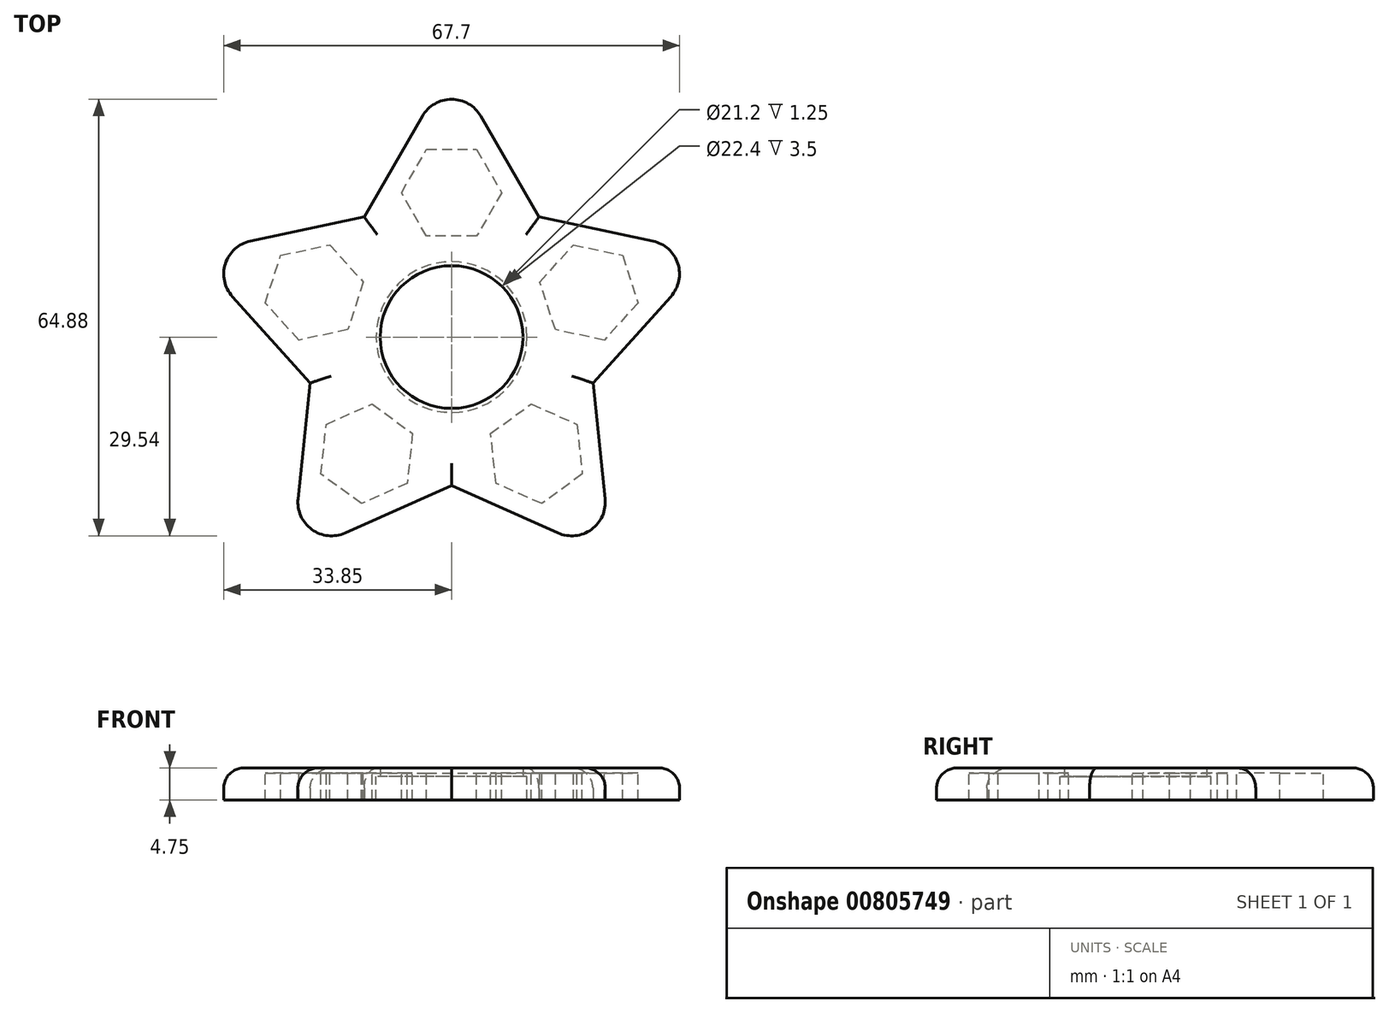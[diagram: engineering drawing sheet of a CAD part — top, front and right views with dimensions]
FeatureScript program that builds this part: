
annotation { "Feature Type Name" : "Feature", "Feature Type Description" : "" }
export const myFeature = defineFeature(function(context is Context, id is Id, definition is map)
    precondition{}
    {
        {
            var Q0;
            Q0=qCreatedBy(makeId("Top.planeOp"),FACE);
            var sketch = newSketch(context, id + "F0", { "sketchPlane" : qUnion([Q0])});
            skCircle(sketch, "E0.cCircle", {"center": v(0, 0) * mm, "radius": 15 * mm, "construction": true});
            skLineSegment(sketch, "E0.0", {"start": v(10.9, -15) * mm, "end": v(-10.9, -15) * mm, "construction": true});
            skLineSegment(sketch, "E0.1", {"start": v(-10.9, -15) * mm, "end": v(-17.63, 5.73) * mm, "construction": true});
            skLineSegment(sketch, "E0.2", {"start": v(-17.63, 5.73) * mm, "end": v(0, 18.54) * mm, "construction": true});
            skLineSegment(sketch, "E0.3", {"start": v(0, 18.54) * mm, "end": v(17.63, 5.73) * mm, "construction": true});
            skLineSegment(sketch, "E0.4", {"start": v(17.63, 5.73) * mm, "end": v(10.9, -15) * mm, "construction": true});
            skPoint(sketch, "E0.0.midPoint", {"position": v(0, -15) * mm});
            skCircle(sketch, "E1", {"center": v(0, 0) * mm, "radius": 11.2 * mm});
            skLineSegment(sketch, "E2", {"start": v(0, 0) * mm, "end": v(-17.63, 5.73) * mm, "construction": true});
            skLineSegment(sketch, "E3", {"start": v(-17.63, 5.73) * mm, "end": v(-45.65, 14.83) * mm, "construction": true});
            skLineSegment(sketch, "E4", {"start": v(0, 0) * mm, "end": v(0, 18.54) * mm, "construction": true});
            skLineSegment(sketch, "E5", {"start": v(0, 18.54) * mm, "end": v(0, 45.62) * mm, "construction": true});
            skLineSegment(sketch, "E6", {"start": v(0, 0) * mm, "end": v(17.63, 5.73) * mm, "construction": true});
            skLineSegment(sketch, "E7", {"start": v(17.63, 5.73) * mm, "end": v(64.66, 21) * mm, "construction": true});
            skLineSegment(sketch, "E8", {"start": v(0, 0) * mm, "end": v(10.9, -15) * mm, "construction": true});
            skLineSegment(sketch, "E9", {"start": v(10.9, -15) * mm, "end": v(33.3, -45.85) * mm, "construction": true});
            skLineSegment(sketch, "E10", {"start": v(0, 0) * mm, "end": v(-10.9, -15) * mm, "construction": true});
            skLineSegment(sketch, "E11", {"start": v(-10.9, -15) * mm, "end": v(-35.87, -49.38) * mm, "construction": true});
            skCircle(sketch, "E12.cCircle", {"center": v(0, 21.45) * mm, "radius": 6.44 * mm, "construction": true});
            skLineSegment(sketch, "E12.0", {"start": v(3.72, 15) * mm, "end": v(-3.72, 15) * mm});
            skLineSegment(sketch, "E12.1", {"start": v(-3.72, 15) * mm, "end": v(-7.44, 21.45) * mm});
            skLineSegment(sketch, "E12.2", {"start": v(-7.44, 21.45) * mm, "end": v(-3.72, 27.9) * mm});
            skLineSegment(sketch, "E12.3", {"start": v(-3.72, 27.9) * mm, "end": v(3.72, 27.89) * mm});
            skLineSegment(sketch, "E12.4", {"start": v(3.72, 27.89) * mm, "end": v(7.44, 21.44) * mm});
            skLineSegment(sketch, "E12.5", {"start": v(7.44, 21.44) * mm, "end": v(3.72, 15) * mm});
            skPoint(sketch, "E12.0.midPoint", {"position": v(0, 15) * mm});
            skCircle(sketch, "E13.cCircle", {"center": v(20.4, 6.63) * mm, "radius": 6.44 * mm, "construction": true});
            skLineSegment(sketch, "E13.0", {"start": v(15.42, 1.1) * mm, "end": v(13.12, 8.17) * mm});
            skLineSegment(sketch, "E13.1", {"start": v(13.12, 8.17) * mm, "end": v(18.1, 13.7) * mm});
            skLineSegment(sketch, "E13.2", {"start": v(18.1, 13.7) * mm, "end": v(25.38, 12.16) * mm});
            skLineSegment(sketch, "E13.3", {"start": v(25.38, 12.16) * mm, "end": v(27.67, 5.08) * mm});
            skLineSegment(sketch, "E13.4", {"start": v(27.67, 5.08) * mm, "end": v(22.7, -0.45) * mm});
            skLineSegment(sketch, "E13.5", {"start": v(22.7, -0.45) * mm, "end": v(15.42, 1.1) * mm});
            skPoint(sketch, "E13.0.midPoint", {"position": v(14.27, 4.64) * mm});
            skCircle(sketch, "E14.cCircle", {"center": v(-20.4, 6.63) * mm, "radius": 6.44 * mm, "construction": true});
            skLineSegment(sketch, "E14.0", {"start": v(-13.12, 8.17) * mm, "end": v(-15.42, 1.1) * mm});
            skLineSegment(sketch, "E14.1", {"start": v(-15.42, 1.1) * mm, "end": v(-22.7, -0.45) * mm});
            skLineSegment(sketch, "E14.2", {"start": v(-22.7, -0.45) * mm, "end": v(-27.67, 5.08) * mm});
            skLineSegment(sketch, "E14.3", {"start": v(-27.67, 5.08) * mm, "end": v(-25.38, 12.16) * mm});
            skLineSegment(sketch, "E14.4", {"start": v(-25.38, 12.16) * mm, "end": v(-18.1, 13.7) * mm});
            skLineSegment(sketch, "E14.5", {"start": v(-18.1, 13.7) * mm, "end": v(-13.12, 8.17) * mm});
            skPoint(sketch, "E14.0.midPoint", {"position": v(-14.27, 4.64) * mm});
            skCircle(sketch, "E15.cCircle", {"center": v(-12.6, -17.35) * mm, "radius": 6.45 * mm, "construction": true});
            skLineSegment(sketch, "E15.0", {"start": v(-11.83, -9.95) * mm, "end": v(-5.8, -14.32) * mm});
            skLineSegment(sketch, "E15.1", {"start": v(-5.8, -14.32) * mm, "end": v(-6.58, -21.72) * mm});
            skLineSegment(sketch, "E15.2", {"start": v(-6.58, -21.72) * mm, "end": v(-13.38, -24.75) * mm});
            skLineSegment(sketch, "E15.3", {"start": v(-13.38, -24.75) * mm, "end": v(-19.4, -20.38) * mm});
            skLineSegment(sketch, "E15.4", {"start": v(-19.4, -20.38) * mm, "end": v(-18.63, -12.98) * mm});
            skLineSegment(sketch, "E15.5", {"start": v(-18.63, -12.98) * mm, "end": v(-11.83, -9.95) * mm});
            skPoint(sketch, "E15.0.midPoint", {"position": v(-8.82, -12.14) * mm});
            skCircle(sketch, "E16.cCircle", {"center": v(12.6, -17.35) * mm, "radius": 6.45 * mm, "construction": true});
            skLineSegment(sketch, "E16.0", {"start": v(5.8, -14.32) * mm, "end": v(11.83, -9.95) * mm});
            skLineSegment(sketch, "E16.1", {"start": v(11.83, -9.95) * mm, "end": v(18.63, -12.98) * mm});
            skLineSegment(sketch, "E16.2", {"start": v(18.63, -12.98) * mm, "end": v(19.4, -20.38) * mm});
            skLineSegment(sketch, "E16.3", {"start": v(19.4, -20.38) * mm, "end": v(13.38, -24.75) * mm});
            skLineSegment(sketch, "E16.4", {"start": v(13.38, -24.75) * mm, "end": v(6.58, -21.72) * mm});
            skLineSegment(sketch, "E16.5", {"start": v(6.58, -21.72) * mm, "end": v(5.8, -14.32) * mm});
            skPoint(sketch, "E16.0.midPoint", {"position": v(8.82, -12.14) * mm});
            skLineSegment(sketch, "E17", {"start": v(-25.38, 12.16) * mm, "end": v(-29.27, 11.33) * mm});
            skLineSegment(sketch, "E18", {"start": v(-30.34, 8.04) * mm, "end": v(-18.47, -5.15) * mm});
            skLineSegment(sketch, "E19", {"start": v(-19.4, -20.38) * mm, "end": v(-17.97, -6.7) * mm});
            skLineSegment(sketch, "E20", {"start": v(-19.4, -20.38) * mm, "end": v(-19.82, -24.33) * mm});
            skLineSegment(sketch, "E21", {"start": v(-17.02, -26.37) * mm, "end": v(-0.81, -19.15) * mm});
            skLineSegment(sketch, "E22", {"start": v(0.81, -19.15) * mm, "end": v(17.02, -26.37) * mm});
            skLineSegment(sketch, "E23", {"start": v(19.82, -24.33) * mm, "end": v(17.97, -6.7) * mm});
            skLineSegment(sketch, "E24", {"start": v(27.67, 5.08) * mm, "end": v(18.47, -5.15) * mm});
            skLineSegment(sketch, "E25", {"start": v(27.67, 5.08) * mm, "end": v(30.34, 8.04) * mm});
            skLineSegment(sketch, "E26", {"start": v(29.27, 11.33) * mm, "end": v(11.92, 15.02) * mm});
            skLineSegment(sketch, "E27", {"start": v(7.44, 21.44) * mm, "end": v(1.73, 31.34) * mm});
            skLineSegment(sketch, "E28", {"start": v(-1.73, 31.34) * mm, "end": v(-10.6, 15.97) * mm});
            skLineSegment(sketch, "E29", {"start": v(-18.1, 13.7) * mm, "end": v(-11.92, 15.02) * mm});
            skLineSegment(sketch, "E30", {"start": v(7.44, 21.44) * mm, "end": v(10.6, 15.97) * mm});
            skPoint(sketch, "E31.visualSharp", {"position": v(-11.05, 15.2) * mm});
            skArc(sketch, "E31.filletArc", {"start": v(-11.92, 15.02) * mm, "mid": v(-11.16, 15.36) * mm, "end": v(-10.6, 15.97) * mm});
            skPoint(sketch, "E32.visualSharp", {"position": v(-32.65, 10.61) * mm});
            skArc(sketch, "E32.filletArc", {"start": v(-29.27, 11.33) * mm, "mid": v(-30.75, 10) * mm, "end": v(-30.34, 8.04) * mm});
            skPoint(sketch, "E33.visualSharp", {"position": v(-17.87, -5.8) * mm});
            skArc(sketch, "E33.filletArc", {"start": v(-17.97, -6.7) * mm, "mid": v(-18.05, -5.87) * mm, "end": v(-18.47, -5.15) * mm});
            skPoint(sketch, "E34.visualSharp", {"position": v(-20.18, -27.78) * mm});
            skArc(sketch, "E34.filletArc", {"start": v(-19.82, -24.33) * mm, "mid": v(-19, -26.16) * mm, "end": v(-17.02, -26.37) * mm});
            skPoint(sketch, "E35.visualSharp", {"position": v(0, -18.8) * mm});
            skArc(sketch, "E35.filletArc", {"start": v(0.81, -19.15) * mm, "mid": v(0, -18.98) * mm, "end": v(-0.81, -19.15) * mm});
            skPoint(sketch, "E36.visualSharp", {"position": v(20.18, -27.78) * mm});
            skArc(sketch, "E36.filletArc", {"start": v(17.02, -26.37) * mm, "mid": v(19, -26.16) * mm, "end": v(19.82, -24.33) * mm});
            skPoint(sketch, "E37.visualSharp", {"position": v(17.87, -5.8) * mm});
            skArc(sketch, "E37.filletArc", {"start": v(18.47, -5.15) * mm, "mid": v(18.05, -5.87) * mm, "end": v(17.97, -6.7) * mm});
            skPoint(sketch, "E38.visualSharp", {"position": v(32.65, 10.61) * mm});
            skArc(sketch, "E38.filletArc", {"start": v(30.34, 8.04) * mm, "mid": v(30.75, 10) * mm, "end": v(29.27, 11.33) * mm});
            skPoint(sketch, "E39.visualSharp", {"position": v(11.05, 15.2) * mm});
            skArc(sketch, "E39.filletArc", {"start": v(10.6, 15.97) * mm, "mid": v(11.16, 15.36) * mm, "end": v(11.92, 15.02) * mm});
            skPoint(sketch, "E40.visualSharp", {"position": v(0, 34.34) * mm});
            skArc(sketch, "E40.filletArc", {"start": v(1.73, 31.34) * mm, "mid": v(0, 32.34) * mm, "end": v(-1.73, 31.34) * mm});
            skLineSegment(sketch, "E41.0", {"start": v(29.89, 14.26) * mm, "end": v(12.98, 17.86) * mm});
            skArc(sketch, "E41.1", {"start": v(32.57, 6.03) * mm, "mid": v(33.6, 10.92) * mm, "end": v(29.89, 14.26) * mm});
            skLineSegment(sketch, "E41.2", {"start": v(29.9, 3.07) * mm, "end": v(32.57, 6.03) * mm});
            skLineSegment(sketch, "E41.3", {"start": v(29.9, 3.07) * mm, "end": v(21, -6.82) * mm});
            skLineSegment(sketch, "E41.4", {"start": v(22.8, -24.02) * mm, "end": v(21, -6.82) * mm});
            skArc(sketch, "E41.5", {"start": v(15.8, -29.1) * mm, "mid": v(20.77, -28.59) * mm, "end": v(22.8, -24.02) * mm});
            skLineSegment(sketch, "E41.6", {"start": v(0, -22.08) * mm, "end": v(15.8, -29.1) * mm});
            skLineSegment(sketch, "E41.7", {"start": v(-15.8, -29.1) * mm, "end": v(0, -22.08) * mm});
            skArc(sketch, "E41.8", {"start": v(-22.8, -24.02) * mm, "mid": v(-20.77, -28.59) * mm, "end": v(-15.8, -29.1) * mm});
            skLineSegment(sketch, "E41.9", {"start": v(-18.72, 16.64) * mm, "end": v(-12.98, 17.86) * mm});
            skLineSegment(sketch, "E41.10", {"start": v(-4.33, 32.84) * mm, "end": v(-12.98, 17.86) * mm});
            skArc(sketch, "E41.11", {"start": v(4.33, 32.84) * mm, "mid": v(0, 35.34) * mm, "end": v(-4.33, 32.84) * mm});
            skLineSegment(sketch, "E41.12", {"start": v(12.98, 17.86) * mm, "end": v(4.33, 32.84) * mm});
            skLineSegment(sketch, "E41.13", {"start": v(-26, 15.1) * mm, "end": v(-18.72, 16.64) * mm});
            skLineSegment(sketch, "E41.14", {"start": v(-26, 15.1) * mm, "end": v(-29.89, 14.26) * mm});
            skArc(sketch, "E41.15", {"start": v(-29.89, 14.26) * mm, "mid": v(-33.6, 10.92) * mm, "end": v(-32.57, 6.03) * mm});
            skLineSegment(sketch, "E41.16", {"start": v(-32.57, 6.03) * mm, "end": v(-21, -6.82) * mm});
            skLineSegment(sketch, "E41.17", {"start": v(-22.39, -20.06) * mm, "end": v(-21, -6.82) * mm});
            skLineSegment(sketch, "E41.18", {"start": v(-22.39, -20.06) * mm, "end": v(-22.8, -24.02) * mm});
            skCircle(sketch, "E42", {"center": v(0, 0) * mm, "radius": 10.6 * mm});
            skSolve(sketch);
        }
        {
            var Q0;
            {var subQ8=sQuery(id+"F0.wireOp",EDGE,"E12.2");Q0=makeQuery(id+"F0.imprint","IMPRINT",FACE,{"disambiguationData":[TD([[makeQuery(id+"F0.imprint","IMPRINT",EDGE,{"derivedFrom":subQ8}),1.0]])]});}
            var Q1;
            Q1=makeQuery(id+"F0.imprint","IMPRINT",FACE,{"disambiguationData":[TD([[makeQuery(id+"F0.imprint","IMPRINT",EDGE,{"derivedFrom":sQuery(id+"F0.wireOp",EDGE,"E1")}),1.0]])]});
            var Q2;
            Q2=makeQuery(id+"F0.imprint","IMPRINT",FACE,{"disambiguationData":[TD([[makeQuery(id+"F0.imprint","IMPRINT",EDGE,{"derivedFrom":sQuery(id+"F0.wireOp",EDGE,"E1")}),-1.0]])]});
            var Q3;
            {var subQ0=sQuery(id+"F0.wireOp",EDGE,"E14.3");Q3=makeQuery(id+"F0.imprint","IMPRINT",FACE,{"disambiguationData":[TD([[makeQuery(id+"F0.imprint","IMPRINT",EDGE,{"derivedFrom":subQ0}),1.0]])]});}
            var Q4;
            Q4=makeQuery(id+"F0.imprint","IMPRINT",FACE,{"disambiguationData":[TD([[makeQuery(id+"F0.imprint","IMPRINT",EDGE,{"derivedFrom":sQuery(id+"F0.wireOp",EDGE,"E14.0")}),-1.0]])]});
            var Q5;
            Q5=makeQuery(id+"F0.imprint","IMPRINT",FACE,{"disambiguationData":[TD([[makeQuery(id+"F0.imprint","IMPRINT",EDGE,{"derivedFrom":sQuery(id+"F0.wireOp",EDGE,"E15.0")}),-1.0]])]});
            var Q6;
            {var subQ0=sQuery(id+"F0.wireOp",EDGE,"E15.3");Q6=makeQuery(id+"F0.imprint","IMPRINT",FACE,{"disambiguationData":[TD([[makeQuery(id+"F0.imprint","IMPRINT",EDGE,{"derivedFrom":subQ0}),1.0]])]});}
            var Q7;
            Q7=makeQuery(id+"F0.imprint","IMPRINT",FACE,{"disambiguationData":[TD([[makeQuery(id+"F0.imprint","IMPRINT",EDGE,{"derivedFrom":sQuery(id+"F0.wireOp",EDGE,"E16.0")}),-1.0]])]});
            var Q8;
            {var subQ0=sQuery(id+"F0.wireOp",EDGE,"E16.3");Q8=makeQuery(id+"F0.imprint","IMPRINT",FACE,{"disambiguationData":[TD([[makeQuery(id+"F0.imprint","IMPRINT",EDGE,{"derivedFrom":subQ0}),1.0]])]});}
            var Q9;
            Q9=makeQuery(id+"F0.imprint","IMPRINT",FACE,{"disambiguationData":[TD([[makeQuery(id+"F0.imprint","IMPRINT",EDGE,{"derivedFrom":sQuery(id+"F0.wireOp",EDGE,"E13.0")}),-1.0]])]});
            var Q10;
            {var subQ0=sQuery(id+"F0.wireOp",EDGE,"E13.3");Q10=makeQuery(id+"F0.imprint","IMPRINT",FACE,{"disambiguationData":[TD([[makeQuery(id+"F0.imprint","IMPRINT",EDGE,{"derivedFrom":subQ0}),1.0]])]});}
            var Q11;
            Q11=makeQuery(id+"F0.imprint","IMPRINT",FACE,{"disambiguationData":[TD([[makeQuery(id+"F0.imprint","IMPRINT",EDGE,{"derivedFrom":sQuery(id+"F0.wireOp",EDGE,"E12.0")}),-1.0]])]});
            var Q12;
            {var subQ0=sQuery(id+"F0.wireOp",EDGE,"E12.3");Q12=makeQuery(id+"F0.imprint","IMPRINT",FACE,{"disambiguationData":[TD([[makeQuery(id+"F0.imprint","IMPRINT",EDGE,{"derivedFrom":subQ0}),1.0]])]});}
            extrude(context, id + "F1", {"entities" : qUnion([Q0, Q1, Q2, Q3, Q4, Q5, Q6, Q7, Q8, Q9, Q10, Q11, Q12]), "depth" : 1.25 * mm, "offsetDistance" : 25 * mm});
        }
        {
            var Q0;
            {var subQ8=sQuery(id+"F0.wireOp",EDGE,"E12.2");Q0=makeQuery(id+"F0.imprint","IMPRINT",FACE,{"disambiguationData":[TD([[makeQuery(id+"F0.imprint","IMPRINT",EDGE,{"derivedFrom":subQ8}),1.0]])]});}
            var Q1;
            {var subQ0=sQuery(id+"F0.wireOp",EDGE,"E13.3");Q1=makeQuery(id+"F0.imprint","IMPRINT",FACE,{"disambiguationData":[TD([[makeQuery(id+"F0.imprint","IMPRINT",EDGE,{"derivedFrom":subQ0}),1.0]])]});}
            var Q2;
            Q2=makeQuery(id+"F0.imprint","IMPRINT",FACE,{"disambiguationData":[TD([[makeQuery(id+"F0.imprint","IMPRINT",EDGE,{"derivedFrom":sQuery(id+"F0.wireOp",EDGE,"E1")}),-1.0]])]});
            var Q3;
            {var subQ0=sQuery(id+"F0.wireOp",EDGE,"E12.3");Q3=makeQuery(id+"F0.imprint","IMPRINT",FACE,{"disambiguationData":[TD([[makeQuery(id+"F0.imprint","IMPRINT",EDGE,{"derivedFrom":subQ0}),1.0]])]});}
            var Q4;
            {var subQ0=sQuery(id+"F0.wireOp",EDGE,"E14.3");Q4=makeQuery(id+"F0.imprint","IMPRINT",FACE,{"disambiguationData":[TD([[makeQuery(id+"F0.imprint","IMPRINT",EDGE,{"derivedFrom":subQ0}),1.0]])]});}
            var Q5;
            {var subQ0=sQuery(id+"F0.wireOp",EDGE,"E15.3");Q5=makeQuery(id+"F0.imprint","IMPRINT",FACE,{"disambiguationData":[TD([[makeQuery(id+"F0.imprint","IMPRINT",EDGE,{"derivedFrom":subQ0}),1.0]])]});}
            var Q6;
            {var subQ0=sQuery(id+"F0.wireOp",EDGE,"E16.3");Q6=makeQuery(id+"F0.imprint","IMPRINT",FACE,{"disambiguationData":[TD([[makeQuery(id+"F0.imprint","IMPRINT",EDGE,{"derivedFrom":subQ0}),1.0]])]});}
            extrude(context, id + "F2", {"entities" : qUnion([Q0, Q1, Q2, Q3, Q4, Q5, Q6]), "operationType" : NewBodyOperationType.ADD, "oppositeDirection" : true, "depth" : 3.5 * mm, "offsetDistance" : 25 * mm});
        }
        {
            var Q0;
            Q0=makeQuery(id+"F1.opExtrude","CAP_EDGE",EDGE,{"disambiguationData":[OSD([sQuery(id+"F0.wireOp",EDGE,"E41.10")])],"isStart":false});
            var Q1;
            Q1=makeQuery(id+"F1.opExtrude","CAP_EDGE",EDGE,{"disambiguationData":[OSD([sQuery(id+"F0.wireOp",EDGE,"E41.9"),sQuery(id+"F0.wireOp",EDGE,"E41.13"),sQuery(id+"F0.wireOp",EDGE,"E41.14")])],"isStart":false});
            var Q2;
            Q2=makeQuery(id+"F1.opExtrude","CAP_EDGE",EDGE,{"disambiguationData":[OSD([sQuery(id+"F0.wireOp",EDGE,"E41.17"),sQuery(id+"F0.wireOp",EDGE,"E41.18")])],"isStart":false});
            var Q3;
            Q3=makeQuery(id+"F1.opExtrude","CAP_EDGE",EDGE,{"disambiguationData":[OSD([sQuery(id+"F0.wireOp",EDGE,"E41.6")])],"isStart":false});
            var Q4;
            Q4=makeQuery(id+"F1.opExtrude","CAP_EDGE",EDGE,{"disambiguationData":[OSD([sQuery(id+"F0.wireOp",EDGE,"E41.2"),sQuery(id+"F0.wireOp",EDGE,"E41.3")])],"isStart":false});
            fillet(context, id + "F3", {"entities" : qUnion([Q0, Q1, Q2, Q3, Q4]), "radius" : 3 * mm, "tangentPropagation" : true, "allowEdgeOverflow" : false});
        }
        {
            var Q0;
            Q0=makeQuery(id+"F2.boolean.opBoolean","SPLIT",FACE,{"disambiguationData":[TD([makeQuery(id+"F2.opExtrude","SWEPT_FACE",FACE,{"disambiguationData":[OSD([sQuery(id+"F0.wireOp",EDGE,"E13.0")])]})])],"derivedFrom":makeQuery(id+"F1.opExtrude","CAP_FACE",FACE,{"disambiguationData":[OSD([sQuery(id+"F0.wireOp",EDGE,"E41.0"),sQuery(id+"F0.wireOp",EDGE,"E41.1"),sQuery(id+"F0.wireOp",EDGE,"E41.2"),sQuery(id+"F0.wireOp",EDGE,"E41.3"),sQuery(id+"F0.wireOp",EDGE,"E41.4"),sQuery(id+"F0.wireOp",EDGE,"E41.5"),sQuery(id+"F0.wireOp",EDGE,"E41.6"),sQuery(id+"F0.wireOp",EDGE,"E41.7"),sQuery(id+"F0.wireOp",EDGE,"E41.8"),sQuery(id+"F0.wireOp",EDGE,"E41.9"),sQuery(id+"F0.wireOp",EDGE,"E41.10"),sQuery(id+"F0.wireOp",EDGE,"E41.11"),sQuery(id+"F0.wireOp",EDGE,"E41.12"),sQuery(id+"F0.wireOp",EDGE,"E41.13"),sQuery(id+"F0.wireOp",EDGE,"E41.14"),sQuery(id+"F0.wireOp",EDGE,"E41.15"),sQuery(id+"F0.wireOp",EDGE,"E41.16"),sQuery(id+"F0.wireOp",EDGE,"E41.17"),sQuery(id+"F0.wireOp",EDGE,"E41.18"),sQuery(id+"F0.wireOp",EDGE,"E42")])],"isStart":true})});
            var Q1;
            Q1=makeQuery(id+"F2.boolean.opBoolean","SPLIT",FACE,{"disambiguationData":[TD([makeQuery(id+"F2.opExtrude","SWEPT_FACE",FACE,{"disambiguationData":[OSD([sQuery(id+"F0.wireOp",EDGE,"E12.0")])]})])],"derivedFrom":makeQuery(id+"F1.opExtrude","CAP_FACE",FACE,{"disambiguationData":[OSD([sQuery(id+"F0.wireOp",EDGE,"E41.0"),sQuery(id+"F0.wireOp",EDGE,"E41.1"),sQuery(id+"F0.wireOp",EDGE,"E41.2"),sQuery(id+"F0.wireOp",EDGE,"E41.3"),sQuery(id+"F0.wireOp",EDGE,"E41.4"),sQuery(id+"F0.wireOp",EDGE,"E41.5"),sQuery(id+"F0.wireOp",EDGE,"E41.6"),sQuery(id+"F0.wireOp",EDGE,"E41.7"),sQuery(id+"F0.wireOp",EDGE,"E41.8"),sQuery(id+"F0.wireOp",EDGE,"E41.9"),sQuery(id+"F0.wireOp",EDGE,"E41.10"),sQuery(id+"F0.wireOp",EDGE,"E41.11"),sQuery(id+"F0.wireOp",EDGE,"E41.12"),sQuery(id+"F0.wireOp",EDGE,"E41.13"),sQuery(id+"F0.wireOp",EDGE,"E41.14"),sQuery(id+"F0.wireOp",EDGE,"E41.15"),sQuery(id+"F0.wireOp",EDGE,"E41.16"),sQuery(id+"F0.wireOp",EDGE,"E41.17"),sQuery(id+"F0.wireOp",EDGE,"E41.18"),sQuery(id+"F0.wireOp",EDGE,"E42")])],"isStart":true})});
            var Q2;
            Q2=makeQuery(id+"F2.boolean.opBoolean","SPLIT",FACE,{"disambiguationData":[TD([makeQuery(id+"F2.opExtrude","SWEPT_FACE",FACE,{"disambiguationData":[OSD([sQuery(id+"F0.wireOp",EDGE,"E14.0")])]})])],"derivedFrom":makeQuery(id+"F1.opExtrude","CAP_FACE",FACE,{"disambiguationData":[OSD([sQuery(id+"F0.wireOp",EDGE,"E41.0"),sQuery(id+"F0.wireOp",EDGE,"E41.1"),sQuery(id+"F0.wireOp",EDGE,"E41.2"),sQuery(id+"F0.wireOp",EDGE,"E41.3"),sQuery(id+"F0.wireOp",EDGE,"E41.4"),sQuery(id+"F0.wireOp",EDGE,"E41.5"),sQuery(id+"F0.wireOp",EDGE,"E41.6"),sQuery(id+"F0.wireOp",EDGE,"E41.7"),sQuery(id+"F0.wireOp",EDGE,"E41.8"),sQuery(id+"F0.wireOp",EDGE,"E41.9"),sQuery(id+"F0.wireOp",EDGE,"E41.10"),sQuery(id+"F0.wireOp",EDGE,"E41.11"),sQuery(id+"F0.wireOp",EDGE,"E41.12"),sQuery(id+"F0.wireOp",EDGE,"E41.13"),sQuery(id+"F0.wireOp",EDGE,"E41.14"),sQuery(id+"F0.wireOp",EDGE,"E41.15"),sQuery(id+"F0.wireOp",EDGE,"E41.16"),sQuery(id+"F0.wireOp",EDGE,"E41.17"),sQuery(id+"F0.wireOp",EDGE,"E41.18"),sQuery(id+"F0.wireOp",EDGE,"E42")])],"isStart":true})});
            var Q3;
            Q3=makeQuery(id+"F2.boolean.opBoolean","SPLIT",FACE,{"disambiguationData":[TD([makeQuery(id+"F2.opExtrude","SWEPT_FACE",FACE,{"disambiguationData":[OSD([sQuery(id+"F0.wireOp",EDGE,"E15.0")])]})])],"derivedFrom":makeQuery(id+"F1.opExtrude","CAP_FACE",FACE,{"disambiguationData":[OSD([sQuery(id+"F0.wireOp",EDGE,"E41.0"),sQuery(id+"F0.wireOp",EDGE,"E41.1"),sQuery(id+"F0.wireOp",EDGE,"E41.2"),sQuery(id+"F0.wireOp",EDGE,"E41.3"),sQuery(id+"F0.wireOp",EDGE,"E41.4"),sQuery(id+"F0.wireOp",EDGE,"E41.5"),sQuery(id+"F0.wireOp",EDGE,"E41.6"),sQuery(id+"F0.wireOp",EDGE,"E41.7"),sQuery(id+"F0.wireOp",EDGE,"E41.8"),sQuery(id+"F0.wireOp",EDGE,"E41.9"),sQuery(id+"F0.wireOp",EDGE,"E41.10"),sQuery(id+"F0.wireOp",EDGE,"E41.11"),sQuery(id+"F0.wireOp",EDGE,"E41.12"),sQuery(id+"F0.wireOp",EDGE,"E41.13"),sQuery(id+"F0.wireOp",EDGE,"E41.14"),sQuery(id+"F0.wireOp",EDGE,"E41.15"),sQuery(id+"F0.wireOp",EDGE,"E41.16"),sQuery(id+"F0.wireOp",EDGE,"E41.17"),sQuery(id+"F0.wireOp",EDGE,"E41.18"),sQuery(id+"F0.wireOp",EDGE,"E42")])],"isStart":true})});
            var Q4;
            Q4=makeQuery(id+"F2.boolean.opBoolean","SPLIT",FACE,{"disambiguationData":[TD([makeQuery(id+"F2.opExtrude","SWEPT_FACE",FACE,{"disambiguationData":[OSD([sQuery(id+"F0.wireOp",EDGE,"E16.0")])]})])],"derivedFrom":makeQuery(id+"F1.opExtrude","CAP_FACE",FACE,{"disambiguationData":[OSD([sQuery(id+"F0.wireOp",EDGE,"E41.0"),sQuery(id+"F0.wireOp",EDGE,"E41.1"),sQuery(id+"F0.wireOp",EDGE,"E41.2"),sQuery(id+"F0.wireOp",EDGE,"E41.3"),sQuery(id+"F0.wireOp",EDGE,"E41.4"),sQuery(id+"F0.wireOp",EDGE,"E41.5"),sQuery(id+"F0.wireOp",EDGE,"E41.6"),sQuery(id+"F0.wireOp",EDGE,"E41.7"),sQuery(id+"F0.wireOp",EDGE,"E41.8"),sQuery(id+"F0.wireOp",EDGE,"E41.9"),sQuery(id+"F0.wireOp",EDGE,"E41.10"),sQuery(id+"F0.wireOp",EDGE,"E41.11"),sQuery(id+"F0.wireOp",EDGE,"E41.12"),sQuery(id+"F0.wireOp",EDGE,"E41.13"),sQuery(id+"F0.wireOp",EDGE,"E41.14"),sQuery(id+"F0.wireOp",EDGE,"E41.15"),sQuery(id+"F0.wireOp",EDGE,"E41.16"),sQuery(id+"F0.wireOp",EDGE,"E41.17"),sQuery(id+"F0.wireOp",EDGE,"E41.18"),sQuery(id+"F0.wireOp",EDGE,"E42")])],"isStart":true})});
            extrude(context, id + "F4", {"entities" : qUnion([Q0, Q1, Q2, Q3, Q4]), "operationType" : NewBodyOperationType.REMOVE, "oppositeDirection" : true, "depth" : .5 * mm, "offsetDistance" : 25 * mm});
        }
    });
